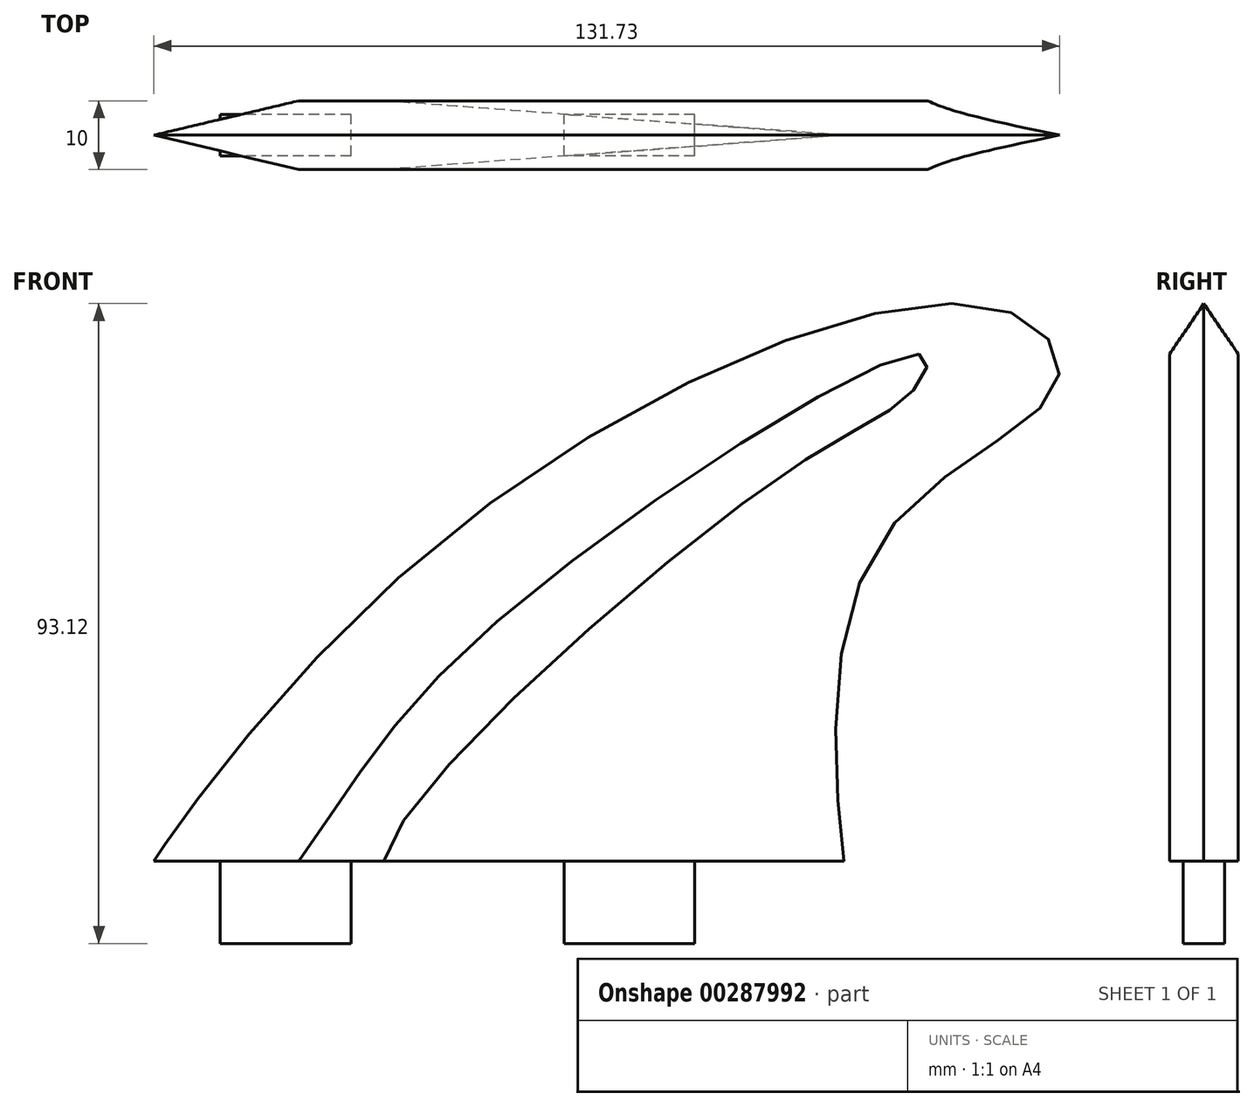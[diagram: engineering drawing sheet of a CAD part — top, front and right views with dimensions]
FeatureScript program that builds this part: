
annotation { "Feature Type Name" : "Feature", "Feature Type Description" : "" }
export const myFeature = defineFeature(function(context is Context, id is Id, definition is map)
    precondition{}
    {
        {
            var Q0;
            Q0=qCreatedBy(makeId("Front.planeOp"),FACE);
            var sketch = newSketch(context, id + "F0", { "sketchPlane" : qUnion([Q0])});
            skLineSegment(sketch, "E0", {"start": v(-33.45, 0) * mm, "end": v(66.9, 0) * mm});
            skFitSpline(sketch, "E1", {"points": [v(-33.45, 0) * mm, v(4.57, 43.4) * mm, v(89.61, 80.33) * mm, v(97.82, 69.14) * mm, v(72.45, 46.76) * mm, v(66.9, 0) * mm], "startDerivative": vector(0, 0) * mm, "endDerivative": vector(21.15, -176.66) * mm});
            skSolve(sketch);
        }
        {
            var Q0;
            Q0=qCreatedBy(makeId("Front.planeOp"),FACE);
            cPlane(context, id + "F1", {"entities" : qUnion([Q0]), "cplaneType" : CPlaneType.OFFSET, "offset" : 5 * mm, "width" : 150 * mm, "height" : 150 * mm});
        }
        {
            var Q0;
            Q0=qCreatedBy(id+"F1.planeOp",FACE);
            var sketch = newSketch(context, id + "F2", { "sketchPlane" : qUnion([Q0])});
            skFitSpline(sketch, "E2", {"points": [v(-12.4, 0) * mm, v(15.03, 33.56) * mm, v(78.5, 73.62) * mm, v(77.5, 69.03) * mm, v(58.19, 56.31) * mm, v(0, 0) * mm], "startDerivative": vector(113.83, 154.6) * mm, "endDerivative": vector(-14.47, -103.18) * mm});
            skLineSegment(sketch, "E3", {"start": v(-12.4, 0) * mm, "end": v(0, 0) * mm});
            skSolve(sketch);
        }
        {
            var Q0;
            Q0=makeQuery(id+"F0.imprint","IMPRINT",FACE,{"disambiguationData":[TD([[makeQuery(id+"F0.imprint","IMPRINT",EDGE,{"derivedFrom":sQuery(id+"F0.wireOp",EDGE,"E0")}),1.0]])]});
            var Q1;
            Q1=makeQuery(id+"F2.imprint","IMPRINT",FACE,{"disambiguationData":[TD([[makeQuery(id+"F2.imprint","IMPRINT",EDGE,{"derivedFrom":sQuery(id+"F2.wireOp",EDGE,"E2")}),-1.0]])]});
            loft(context, id + "F3", {"sheetProfilesArray" : [{ "sheetProfileEntities" : qUnion([Q0]) }, { "sheetProfileEntities" : qUnion([Q1]) }]});
        }
        {
            var Q0;
            Q0=makeQuery(id+"F3.opLoft","SWEPT_BODY",BODY,{"disambiguationData":[OSD([makeQuery(id+"F0.imprint","IMPRINT",FACE,{"disambiguationData":[TD([[makeQuery(id+"F0.imprint","IMPRINT",EDGE,{"derivedFrom":sQuery(id+"F0.wireOp",EDGE,"E0")}),1.0]])]}),makeQuery(id+"F2.imprint","IMPRINT",FACE,{"disambiguationData":[TD([[makeQuery(id+"F2.imprint","IMPRINT",EDGE,{"derivedFrom":sQuery(id+"F2.wireOp",EDGE,"E2")}),-1.0]])]})])]});
            var Q1;
            Q1=qCreatedBy(makeId("Front.planeOp"),FACE);
            mirror(context, id + "F4", {"operationType" : NewBodyOperationType.ADD, "entities" : qUnion([Q0]), "mirrorPlane" : qUnion([Q1])});
        }
        {
            var Q0;
            Q0=qCreatedBy(makeId("Front.planeOp"),FACE);
            var sketch = newSketch(context, id + "F5", { "sketchPlane" : qUnion([Q0])});
            skLineSegment(sketch, "E4.bottom", {"start": v(45.2, 0) * mm, "end": v(26.2, 0) * mm});
            skLineSegment(sketch, "E4.top", {"start": v(45.2, -12) * mm, "end": v(26.2, -12) * mm});
            skLineSegment(sketch, "E4.left", {"start": v(45.2, 0) * mm, "end": v(45.2, -12) * mm});
            skLineSegment(sketch, "E4.right", {"start": v(26.2, 0) * mm, "end": v(26.2, -12) * mm});
            skLineSegment(sketch, "E5.bottom", {"start": v(-4.8, 0) * mm, "end": v(-23.8, 0) * mm});
            skLineSegment(sketch, "E5.top", {"start": v(-4.8, -12) * mm, "end": v(-23.8, -12) * mm});
            skLineSegment(sketch, "E5.left", {"start": v(-4.8, 0) * mm, "end": v(-4.8, -12) * mm});
            skLineSegment(sketch, "E5.right", {"start": v(-23.8, 0) * mm, "end": v(-23.8, -12) * mm});
            skSolve(sketch);
        }
        {
            var Q0;
            Q0=makeQuery(id+"F5.imprint","IMPRINT",FACE,{"disambiguationData":[TD([[makeQuery(id+"F5.imprint","IMPRINT",EDGE,{"derivedFrom":sQuery(id+"F5.wireOp",EDGE,"E4.bottom")}),1.0]])]});
            var Q1;
            Q1=makeQuery(id+"F5.imprint","IMPRINT",FACE,{"disambiguationData":[TD([[makeQuery(id+"F5.imprint","IMPRINT",EDGE,{"derivedFrom":sQuery(id+"F5.wireOp",EDGE,"E5.bottom")}),1.0]])]});
            extrude(context, id + "F6", {"entities" : qUnion([Q0, Q1]), "operationType" : NewBodyOperationType.ADD, "endBound" : BoundingType.SYMMETRIC, "depth" : 6 * mm});
        }
    });
